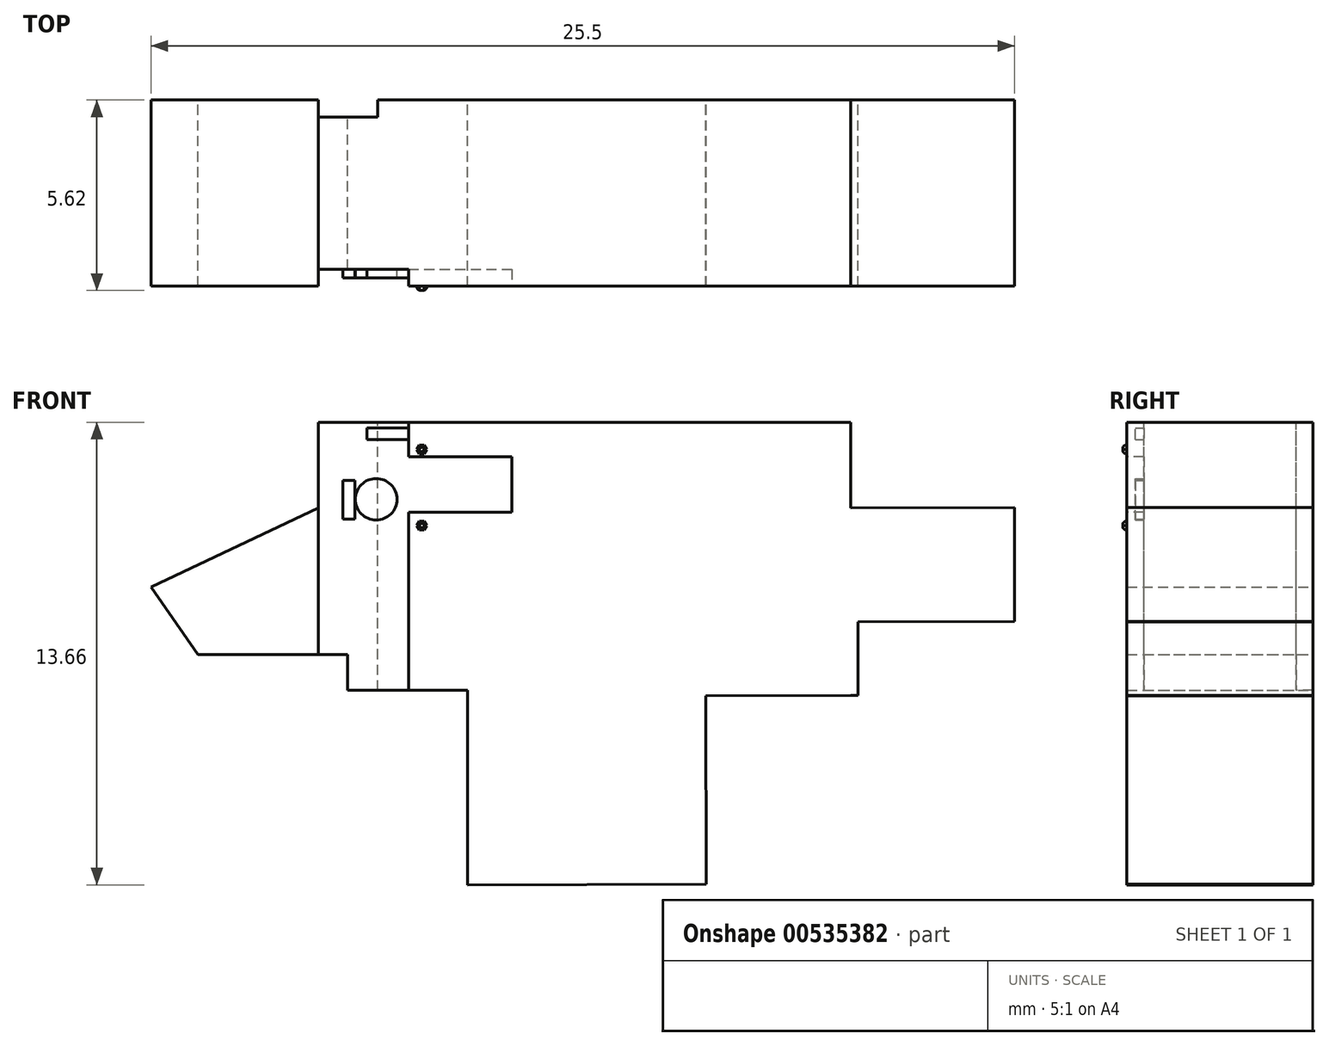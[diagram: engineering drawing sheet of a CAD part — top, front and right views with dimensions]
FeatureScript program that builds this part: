
annotation { "Feature Type Name" : "Feature", "Feature Type Description" : "" }
export const myFeature = defineFeature(function(context is Context, id is Id, definition is map)
    precondition{}
    {
        {
            var Q0;
            Q0=qCreatedBy(makeId("Front.planeOp"),FACE);
            var sketch = newSketch(context, id + "F0", { "sketchPlane" : qUnion([Q0])});
            skLineSegment(sketch, "E0", {"start": v(-12.75, 0) * mm, "end": v(-11.36, -2) * mm});
            skLineSegment(sketch, "E1", {"start": v(-7.8, 2.34) * mm, "end": v(-12.75, 0) * mm});
            skLineSegment(sketch, "E2", {"start": v(6.48, 4.86) * mm, "end": v(7.91, 4.86) * mm});
            skLineSegment(sketch, "E3", {"start": v(7.91, 4.86) * mm, "end": v(7.91, 4.33) * mm});
            skLineSegment(sketch, "E4", {"start": v(7.91, 4.33) * mm, "end": v(7.92, 2.33) * mm});
            skLineSegment(sketch, "E5", {"start": v(7.92, 2.33) * mm, "end": v(12.75, 2.35) * mm});
            skPoint(sketch, "E5.endSnap0", {"position": v(12.75, 0) * mm});
            skLineSegment(sketch, "E6", {"start": v(12.75, 2.35) * mm, "end": v(12.75, -1.02) * mm});
            skLineSegment(sketch, "E7", {"start": v(12.75, -1.02) * mm, "end": v(8.13, -1.04) * mm});
            skLineSegment(sketch, "E8", {"start": v(7.91, -3.2) * mm, "end": v(3.63, -3.22) * mm});
            skLineSegment(sketch, "E9", {"start": v(3.63, -3.22) * mm, "end": v(3.65, -8.78) * mm});
            skLineSegment(sketch, "E10", {"start": v(3.65, -8.78) * mm, "end": v(-3.4, -8.8) * mm});
            skLineSegment(sketch, "E11", {"start": v(-3.4, -8.8) * mm, "end": v(-3.4, -3.06) * mm});
            skLineSegment(sketch, "E12", {"start": v(-7.8, 2.34) * mm, "end": v(-7.8, 3.2) * mm});
            skLineSegment(sketch, "E13", {"start": v(-7.8, 3.2) * mm, "end": v(-7.8, 4.86) * mm});
            skPoint(sketch, "E13.endSnap0", {"position": v(7.2, 4.86) * mm});
            skLineSegment(sketch, "E14", {"start": v(-7.8, 4.86) * mm, "end": v(6.48, 4.86) * mm});
            skLineSegment(sketch, "E15", {"start": v(-11.36, -2) * mm, "end": v(-6.94, -2) * mm});
            skLineSegment(sketch, "E16", {"start": v(-6.94, -2) * mm, "end": v(-6.94, -3.06) * mm});
            skLineSegment(sketch, "E17", {"start": v(-6.94, -3.06) * mm, "end": v(-3.4, -3.06) * mm});
            skLineSegment(sketch, "E18", {"start": v(8.13, -1.04) * mm, "end": v(8.13, -3.2) * mm});
            skLineSegment(sketch, "E19", {"start": v(8.13, -3.2) * mm, "end": v(7.91, -3.2) * mm});
            skSolve(sketch);
        }
        {
            var Q0;
            Q0 = qSketchRegion(id + "F0", true);
            extrude(context, id + "F1", {"entities" : qUnion([Q0]), "depth" : 5.5 * mm, "offsetDistance" : 25 * mm});
        }
        {
            var Q0;
            Q0=makeQuery(id+"F1.opExtrude","SWEPT_FACE",FACE,{"disambiguationData":[OSD([sQuery(id+"F0.wireOp",EDGE,"E2"),sQuery(id+"F0.wireOp",EDGE,"E14")])]});
            var sketch = newSketch(context, id + "F2", { "sketchPlane" : qUnion([Q0])});
            skLineSegment(sketch, "E20.bottom", {"start": v(-7.8, 0) * mm, "end": v(-6.06, 0) * mm});
            skLineSegment(sketch, "E20.top", {"start": v(-7.8, -0.5) * mm, "end": v(-6.06, -0.5) * mm});
            skLineSegment(sketch, "E20.left", {"start": v(-7.8, 0) * mm, "end": v(-7.8, -0.5) * mm});
            skLineSegment(sketch, "E20.right", {"start": v(-6.06, 0) * mm, "end": v(-6.06, -0.5) * mm});
            skLineSegment(sketch, "E21.bottom", {"start": v(-7.8, -5.5) * mm, "end": v(-5.15, -5.5) * mm});
            skLineSegment(sketch, "E21.top", {"start": v(-7.8, -5) * mm, "end": v(-5.15, -5) * mm});
            skLineSegment(sketch, "E21.left", {"start": v(-7.8, -5.5) * mm, "end": v(-7.8, -5) * mm});
            skLineSegment(sketch, "E21.right", {"start": v(-5.15, -5.5) * mm, "end": v(-5.15, -5) * mm});
            skSolve(sketch);
        }
        {
            var Q0;
            Q0 = qSketchRegion(id + "F2", true);
            extrude(context, id + "F3", {"entities" : qUnion([Q0]), "operationType" : NewBodyOperationType.REMOVE, "oppositeDirection" : true, "depth" : 25 * mm, "offsetDistance" : 25 * mm});
        }
        {
            var Q0;
            {var subQ0=sQuery(id+"F0.wireOp",EDGE,"E11");var subQ1=sQuery(id+"F0.wireOp",EDGE,"E10");var subQ2=sQuery(id+"F0.wireOp",EDGE,"E9");var subQ3=sQuery(id+"F0.wireOp",EDGE,"E8");var subQ4=sQuery(id+"F0.wireOp",EDGE,"E7");var subQ5=sQuery(id+"F0.wireOp",EDGE,"E14");var subQ6=sQuery(id+"F0.wireOp",EDGE,"E2");var subQ7=sQuery(id+"F0.wireOp",EDGE,"E17");var subQ8=sQuery(id+"F0.wireOp",EDGE,"E4");var subQ9=sQuery(id+"F0.wireOp",EDGE,"E3");var subQ10=sQuery(id+"F0.wireOp",EDGE,"E5");var subQ11=sQuery(id+"F0.wireOp",EDGE,"E6");var subQ12=sQuery(id+"F0.wireOp",EDGE,"E18");var subQ13=sQuery(id+"F0.wireOp",EDGE,"E19");Q0=makeQuery(id+"F3.boolean.opBoolean","SPLIT",FACE,{"disambiguationData":[TD([makeQuery(id+"F1.opExtrude","SWEPT_FACE",FACE,{"disambiguationData":[OSD([subQ10])]})])],"derivedFrom":makeQuery(id+"F1.opExtrude","CAP_FACE",FACE,{"disambiguationData":[OSD([sQuery(id+"F0.wireOp",EDGE,"E0"),sQuery(id+"F0.wireOp",EDGE,"E1"),subQ6,subQ9,subQ8,subQ10,subQ11,subQ4,subQ3,subQ2,subQ1,subQ0,sQuery(id+"F0.wireOp",EDGE,"E12"),sQuery(id+"F0.wireOp",EDGE,"E13"),subQ5,sQuery(id+"F0.wireOp",EDGE,"E15"),sQuery(id+"F0.wireOp",EDGE,"E16"),subQ7,subQ12,subQ13])],"isStart":false})});}
            var sketch = newSketch(context, id + "F4", { "sketchPlane" : qUnion([Q0])});
            skLineSegment(sketch, "E22.bottom", {"start": v(-5.15, 3.84) * mm, "end": v(-2.1, 3.84) * mm});
            skLineSegment(sketch, "E22.top", {"start": v(-5.15, 2.2) * mm, "end": v(-2.1, 2.2) * mm});
            skLineSegment(sketch, "E22.left", {"start": v(-5.15, 3.84) * mm, "end": v(-5.15, 2.2) * mm});
            skLineSegment(sketch, "E22.right", {"start": v(-2.1, 3.84) * mm, "end": v(-2.1, 2.2) * mm});
            skSolve(sketch);
        }
        {
            var Q0;
            Q0 = qSketchRegion(id + "F4", true);
            extrude(context, id + "F5", {"entities" : qUnion([Q0]), "operationType" : NewBodyOperationType.REMOVE, "oppositeDirection" : true, "depth" : .5 * mm, "offsetDistance" : 25 * mm});
        }
        {
            var Q0;
            Q0=makeQuery(id+"F5.boolean.opBoolean","MERGE",FACE,{"derivedFrom":[makeQuery(id+"F3.boolean.opBoolean","COPY",FACE,{"derivedFrom":makeQuery(id+"F3.opExtrude","SWEPT_FACE",FACE,{"disambiguationData":[OSD([sQuery(id+"F2.wireOp",EDGE,"E21.top")])]})}),makeQuery(id+"F5.opExtrude","CAP_FACE",FACE,{"disambiguationData":[OSD([sQuery(id+"F4.wireOp",EDGE,"E22.bottom"),sQuery(id+"F4.wireOp",EDGE,"E22.top"),sQuery(id+"F4.wireOp",EDGE,"E22.left"),sQuery(id+"F4.wireOp",EDGE,"E22.right")])],"isStart":false})]});
            var sketch = newSketch(context, id + "F6", { "sketchPlane" : qUnion([Q0])});
            skCircle(sketch, "E23", {"center": v(-6.1, 2.59) * mm, "radius": 0.61 * mm});
            skLineSegment(sketch, "E24.bottom", {"start": v(-7.08, 3.15) * mm, "end": v(-6.73, 3.15) * mm});
            skLineSegment(sketch, "E24.top", {"start": v(-7.08, 2) * mm, "end": v(-6.73, 2) * mm});
            skLineSegment(sketch, "E24.left", {"start": v(-7.08, 3.15) * mm, "end": v(-7.08, 2) * mm});
            skLineSegment(sketch, "E24.right", {"start": v(-6.73, 3.15) * mm, "end": v(-6.73, 2) * mm});
            skPoint(sketch, "E25.oppositeSnap0", {"position": v(-5.15, 4.35) * mm});
            skLineSegment(sketch, "E25.bottom", {"start": v(-5.15, 4.7) * mm, "end": v(-6.38, 4.7) * mm});
            skLineSegment(sketch, "E25.top", {"start": v(-5.15, 4.35) * mm, "end": v(-6.38, 4.35) * mm});
            skLineSegment(sketch, "E25.left", {"start": v(-5.15, 4.7) * mm, "end": v(-5.15, 4.35) * mm});
            skLineSegment(sketch, "E25.right", {"start": v(-6.38, 4.7) * mm, "end": v(-6.38, 4.35) * mm});
            skSolve(sketch);
        }
        {
            var Q0;
            Q0 = qSketchRegion(id + "F6", true);
            extrude(context, id + "F7", {"entities" : qUnion([Q0]), "operationType" : NewBodyOperationType.ADD, "depth" : .25 * mm, "offsetDistance" : 25 * mm});
        }
        {
            var Q0;
            {var subQ0=sQuery(id+"F0.wireOp",EDGE,"E11");var subQ1=sQuery(id+"F0.wireOp",EDGE,"E10");var subQ2=sQuery(id+"F0.wireOp",EDGE,"E9");var subQ3=sQuery(id+"F0.wireOp",EDGE,"E8");var subQ4=sQuery(id+"F0.wireOp",EDGE,"E7");var subQ5=sQuery(id+"F0.wireOp",EDGE,"E14");var subQ6=sQuery(id+"F0.wireOp",EDGE,"E2");var subQ7=sQuery(id+"F0.wireOp",EDGE,"E17");var subQ8=sQuery(id+"F0.wireOp",EDGE,"E4");var subQ9=sQuery(id+"F0.wireOp",EDGE,"E3");var subQ10=sQuery(id+"F0.wireOp",EDGE,"E5");var subQ11=sQuery(id+"F0.wireOp",EDGE,"E6");var subQ12=sQuery(id+"F0.wireOp",EDGE,"E18");var subQ13=sQuery(id+"F0.wireOp",EDGE,"E19");Q0=makeQuery(id+"F3.boolean.opBoolean","SPLIT",FACE,{"disambiguationData":[TD([makeQuery(id+"F1.opExtrude","SWEPT_FACE",FACE,{"disambiguationData":[OSD([subQ10])]})])],"derivedFrom":makeQuery(id+"F1.opExtrude","CAP_FACE",FACE,{"disambiguationData":[OSD([sQuery(id+"F0.wireOp",EDGE,"E0"),sQuery(id+"F0.wireOp",EDGE,"E1"),subQ6,subQ9,subQ8,subQ10,subQ11,subQ4,subQ3,subQ2,subQ1,subQ0,sQuery(id+"F0.wireOp",EDGE,"E12"),sQuery(id+"F0.wireOp",EDGE,"E13"),subQ5,sQuery(id+"F0.wireOp",EDGE,"E15"),sQuery(id+"F0.wireOp",EDGE,"E16"),subQ7,subQ12,subQ13])],"isStart":false})});}
            var sketch = newSketch(context, id + "F8", { "sketchPlane" : qUnion([Q0])});
            skCircle(sketch, "E26.cCircle", {"center": v(-4.76, 4.06) * mm, "radius": 0.12 * mm, "construction": true});
            skLineSegment(sketch, "E26.0", {"start": v(-4.68, 3.94) * mm, "end": v(-4.83, 3.94) * mm});
            skLineSegment(sketch, "E26.1", {"start": v(-4.83, 3.94) * mm, "end": v(-4.9, 4.06) * mm});
            skLineSegment(sketch, "E26.2", {"start": v(-4.9, 4.06) * mm, "end": v(-4.83, 4.19) * mm});
            skLineSegment(sketch, "E26.3", {"start": v(-4.83, 4.19) * mm, "end": v(-4.68, 4.19) * mm});
            skLineSegment(sketch, "E26.4", {"start": v(-4.68, 4.19) * mm, "end": v(-4.61, 4.06) * mm});
            skLineSegment(sketch, "E26.5", {"start": v(-4.61, 4.06) * mm, "end": v(-4.68, 3.94) * mm});
            skPoint(sketch, "E26.0.midPoint", {"position": v(-4.75, 3.94) * mm});
            skCircle(sketch, "E27.cCircle", {"center": v(-4.76, 1.81) * mm, "radius": 0.12 * mm, "construction": true});
            skLineSegment(sketch, "E27.0", {"start": v(-4.68, 1.69) * mm, "end": v(-4.83, 1.69) * mm});
            skLineSegment(sketch, "E27.1", {"start": v(-4.83, 1.69) * mm, "end": v(-4.9, 1.81) * mm});
            skLineSegment(sketch, "E27.2", {"start": v(-4.9, 1.81) * mm, "end": v(-4.83, 1.94) * mm});
            skLineSegment(sketch, "E27.3", {"start": v(-4.83, 1.94) * mm, "end": v(-4.68, 1.94) * mm});
            skLineSegment(sketch, "E27.4", {"start": v(-4.68, 1.94) * mm, "end": v(-4.61, 1.81) * mm});
            skLineSegment(sketch, "E27.5", {"start": v(-4.61, 1.81) * mm, "end": v(-4.68, 1.69) * mm});
            skPoint(sketch, "E27.0.midPoint", {"position": v(-4.76, 1.69) * mm});
            skSolve(sketch);
        }
        {
            var Q0;
            Q0 = qSketchRegion(id + "F8", true);
            extrude(context, id + "F9", {"entities" : qUnion([Q0]), "operationType" : NewBodyOperationType.ADD, "depth" : .125 * mm, "offsetDistance" : 25 * mm});
        }
        {
            var Q0;
            Q0=makeQuery(id+"F9.opExtrude","CAP_EDGE",EDGE,{"disambiguationData":[OSD([sQuery(id+"F8.wireOp",EDGE,"E26.2")])],"isStart":false});
            var Q1;
            Q1=makeQuery(id+"F9.opExtrude","CAP_EDGE",EDGE,{"disambiguationData":[OSD([sQuery(id+"F8.wireOp",EDGE,"E26.1")])],"isStart":false});
            var Q2;
            Q2=makeQuery(id+"F9.opExtrude","CAP_EDGE",EDGE,{"disambiguationData":[OSD([sQuery(id+"F8.wireOp",EDGE,"E26.0")])],"isStart":false});
            var Q3;
            Q3=makeQuery(id+"F9.opExtrude","CAP_EDGE",EDGE,{"disambiguationData":[OSD([sQuery(id+"F8.wireOp",EDGE,"E26.4")])],"isStart":false});
            var Q4;
            Q4=makeQuery(id+"F9.opExtrude","CAP_EDGE",EDGE,{"disambiguationData":[OSD([sQuery(id+"F8.wireOp",EDGE,"E26.3")])],"isStart":false});
            var Q5;
            Q5=makeQuery(id+"F9.opExtrude","CAP_EDGE",EDGE,{"disambiguationData":[OSD([sQuery(id+"F8.wireOp",EDGE,"E26.5")])],"isStart":false});
            var Q6;
            Q6=makeQuery(id+"F9.opExtrude","CAP_EDGE",EDGE,{"disambiguationData":[OSD([sQuery(id+"F8.wireOp",EDGE,"E27.3")])],"isStart":false});
            var Q7;
            Q7=makeQuery(id+"F9.opExtrude","CAP_EDGE",EDGE,{"disambiguationData":[OSD([sQuery(id+"F8.wireOp",EDGE,"E27.4")])],"isStart":false});
            var Q8;
            Q8=makeQuery(id+"F9.opExtrude","CAP_EDGE",EDGE,{"disambiguationData":[OSD([sQuery(id+"F8.wireOp",EDGE,"E27.5")])],"isStart":false});
            var Q9;
            Q9=makeQuery(id+"F9.opExtrude","CAP_EDGE",EDGE,{"disambiguationData":[OSD([sQuery(id+"F8.wireOp",EDGE,"E27.0")])],"isStart":false});
            var Q10;
            Q10=makeQuery(id+"F9.opExtrude","CAP_EDGE",EDGE,{"disambiguationData":[OSD([sQuery(id+"F8.wireOp",EDGE,"E27.1")])],"isStart":false});
            var Q11;
            Q11=makeQuery(id+"F9.opExtrude","CAP_EDGE",EDGE,{"disambiguationData":[OSD([sQuery(id+"F8.wireOp",EDGE,"E27.2")])],"isStart":false});
            fillet(context, id + "F10", {"entities" : qUnion([Q0, Q1, Q2, Q3, Q4, Q5, Q6, Q7, Q8, Q9, Q10, Q11]), "radius" : .1 * mm, "tangentPropagation" : true, "allowEdgeOverflow" : false});
        }
    });
